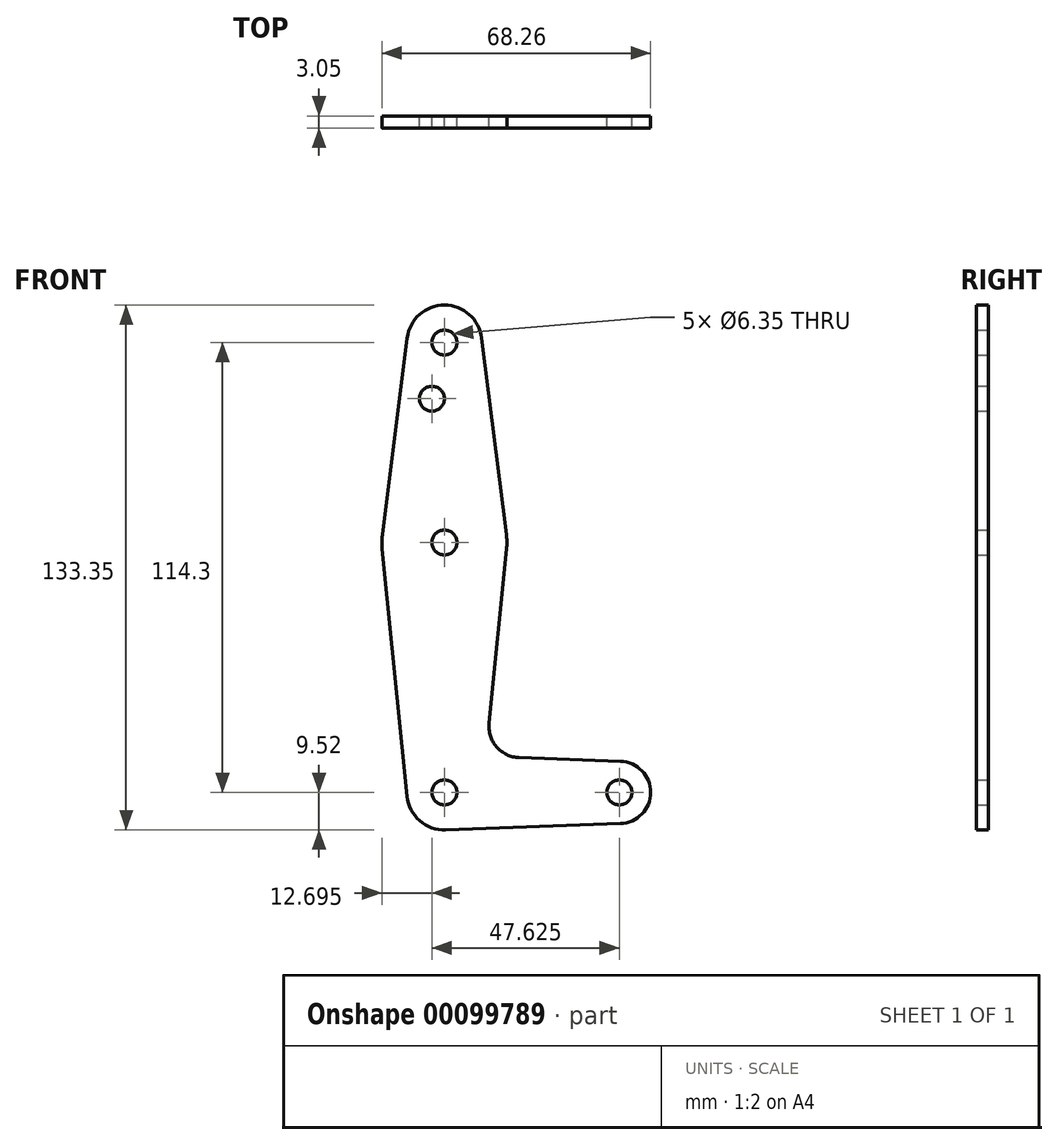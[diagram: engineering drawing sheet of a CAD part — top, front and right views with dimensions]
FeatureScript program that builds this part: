
annotation { "Feature Type Name" : "Feature", "Feature Type Description" : "" }
export const myFeature = defineFeature(function(context is Context, id is Id, definition is map)
    precondition{}
    {
        {
            var Q0;
            Q0=qCreatedBy(makeId("Front.planeOp"),FACE);
            var sketch = newSketch(context, id + "F0", { "sketchPlane" : qUnion([Q0])});
            skLineSegment(sketch, "E0", {"start": v(0, 114.3) * mm, "end": v(0, 0) * mm, "construction": true});
            skCircle(sketch, "E1", {"center": v(0, 114.3) * mm, "radius": 9.53 * mm});
            skCircle(sketch, "E2", {"center": v(0, 63.5) * mm, "radius": 15.88 * mm});
            skCircle(sketch, "E3", {"center": v(0, 0) * mm, "radius": 9.53 * mm});
            skLineSegment(sketch, "E4", {"start": v(0, 0) * mm, "end": v(44.45, 0) * mm, "construction": true});
            skCircle(sketch, "E5", {"center": v(44.45, 0) * mm, "radius": 7.94 * mm});
            skLineSegment(sketch, "E6", {"start": v(-15.75, 65.48) * mm, "end": v(-9.45, 115.5) * mm});
            skLineSegment(sketch, "E7", {"start": v(9.45, 115.5) * mm, "end": v(15.75, 65.48) * mm});
            skLineSegment(sketch, "E8", {"start": v(15.8, 61.91) * mm, "end": v(11.34, 17.6) * mm});
            skLineSegment(sketch, "E9", {"start": v(-15.8, 61.91) * mm, "end": v(-9.48, -0.95) * mm});
            skCircle(sketch, "E10", {"center": v(0, 114.3) * mm, "radius": 3.18 * mm});
            skCircle(sketch, "E11", {"center": v(-3.18, 100.03) * mm, "radius": 3.18 * mm});
            skCircle(sketch, "E12", {"center": v(0, 63.5) * mm, "radius": 3.18 * mm});
            skCircle(sketch, "E13", {"center": v(0, 0) * mm, "radius": 3.18 * mm});
            skCircle(sketch, "E14", {"center": v(44.45, 0) * mm, "radius": 3.18 * mm});
            skLineSegment(sketch, "E15", {"start": v(18.97, 8.85) * mm, "end": v(44.73, 7.93) * mm});
            skArc(sketch, "E16.filletArc", {"start": v(11.34, 17.6) * mm, "mid": v(13.26, 11.57) * mm, "end": v(18.97, 8.85) * mm});
            skLineSegment(sketch, "E17", {"start": v(0.34, -9.52) * mm, "end": v(44.73, -7.93) * mm});
            skSolve(sketch);
        }
        {
            var Q0;
            Q0=makeQuery(id+"F0.imprint","IMPRINT",FACE,{"disambiguationData":[TD([[makeQuery(id+"F0.imprint","IMPRINT",EDGE,{"derivedFrom":sQuery(id+"F0.wireOp",EDGE,"E10")}),-1.0]])]});
            var Q1;
            {var subQ1=sQuery(id+"F0.wireOp",EDGE,"E6");Q1=makeQuery(id+"F0.imprint","IMPRINT",FACE,{"disambiguationData":[TD([[makeQuery(id+"F0.imprint","IMPRINT",EDGE,{"derivedFrom":subQ1}),-1.0]])]});}
            var Q2;
            Q2=makeQuery(id+"F0.imprint","IMPRINT",FACE,{"disambiguationData":[TD([[makeQuery(id+"F0.imprint","IMPRINT",EDGE,{"derivedFrom":sQuery(id+"F0.wireOp",EDGE,"E12")}),-1.0]])]});
            var Q3;
            {var subQ0=sQuery(id+"F0.wireOp",EDGE,"E8");Q3=makeQuery(id+"F0.imprint","IMPRINT",FACE,{"disambiguationData":[TD([[makeQuery(id+"F0.imprint","IMPRINT",EDGE,{"derivedFrom":subQ0}),-1.0]])]});}
            var Q4;
            Q4=makeQuery(id+"F0.imprint","IMPRINT",FACE,{"disambiguationData":[TD([[makeQuery(id+"F0.imprint","IMPRINT",EDGE,{"derivedFrom":sQuery(id+"F0.wireOp",EDGE,"E13")}),-1.0]])]});
            var Q5;
            Q5=makeQuery(id+"F0.imprint","IMPRINT",FACE,{"disambiguationData":[TD([[makeQuery(id+"F0.imprint","IMPRINT",EDGE,{"derivedFrom":sQuery(id+"F0.wireOp",EDGE,"E14")}),-1.0]])]});
            extrude(context, id + "F1", {"entities" : qUnion([Q0, Q1, Q2, Q3, Q4, Q5]), "depth" : 3.05 * mm});
        }
    });
